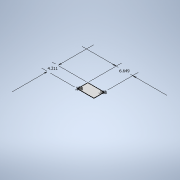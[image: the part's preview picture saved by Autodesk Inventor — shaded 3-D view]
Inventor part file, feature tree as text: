
AUTODESK INVENTOR PART (.ipt)
format: ipt  version: 2020 (Build 240168000, 168)  size: 106,496 bytes
history: native  units: in
note: dims shown in document units (in); Inventor stores cm internally (conversion verified against a paired STEP export)
features: sketch x1, extrude x1, hole x1
ambient origin geometry x8: Origin, YZ Plane, XZ Plane, XY Plane, X Axis, Y Axis, Z Axis, Center Point
bodies: Solid1 (feature_tree)
feature tree (3):
  sketch  "Sketch1"  dims[d0=6.6486in d1=4.2106in d2=0.1678in d3=0.1678in d4=0.1678in d5=0.1678in d6=0.0625in d7=0.0in d8=0.129in d9=0.224in d10=0.225in d11=0.0625in d12=0.5635in d13=0.349in d14=0.8108in]
  extrude  "Extrusion1"  Depth=4.2106in
  hole  "Hole1"  [1 undecoded]
note: 1 required parameter value undecoded (feature->parameter linkage not recoverable at this tier; creation-order binding heuristic only, values carry confidence <= 0.55)
